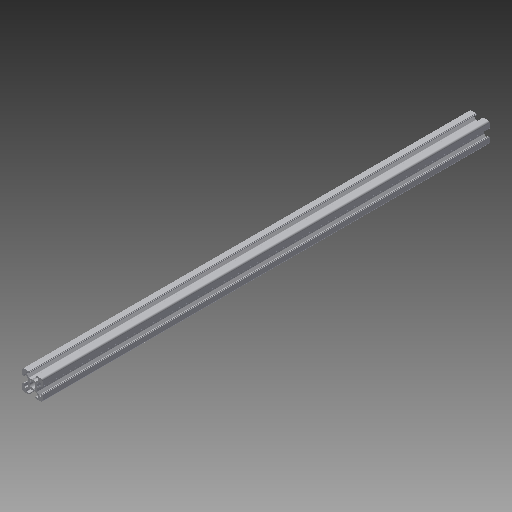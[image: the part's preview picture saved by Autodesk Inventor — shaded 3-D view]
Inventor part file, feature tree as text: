
AUTODESK INVENTOR PART (.ipt)
format: ipt  version: 2019 (Build 230136000, 136)  size: 311,296 bytes
history: native  units: in
note: dims shown in document units (in); Inventor stores cm internally (conversion verified against a paired STEP export)
features: other x3, extrude x1, sketch x1
ambient origin geometry x8: Origin, YZ Plane, XZ Plane, XY Plane, X Axis, Y Axis, Z Axis, Center Point
bodies: Solid1 (feature_tree)
feature tree (5):
  other  "Blocks"
  extrude  "Extrusion1"  [1 undecoded]
  sketch  "Sketch1"  dims[d1=0.0in]
  other  "20x20"
  other  "20x20:1"
note: 1 required parameter value undecoded (feature->parameter linkage not recoverable at this tier; creation-order binding heuristic only, values carry confidence <= 0.55)
